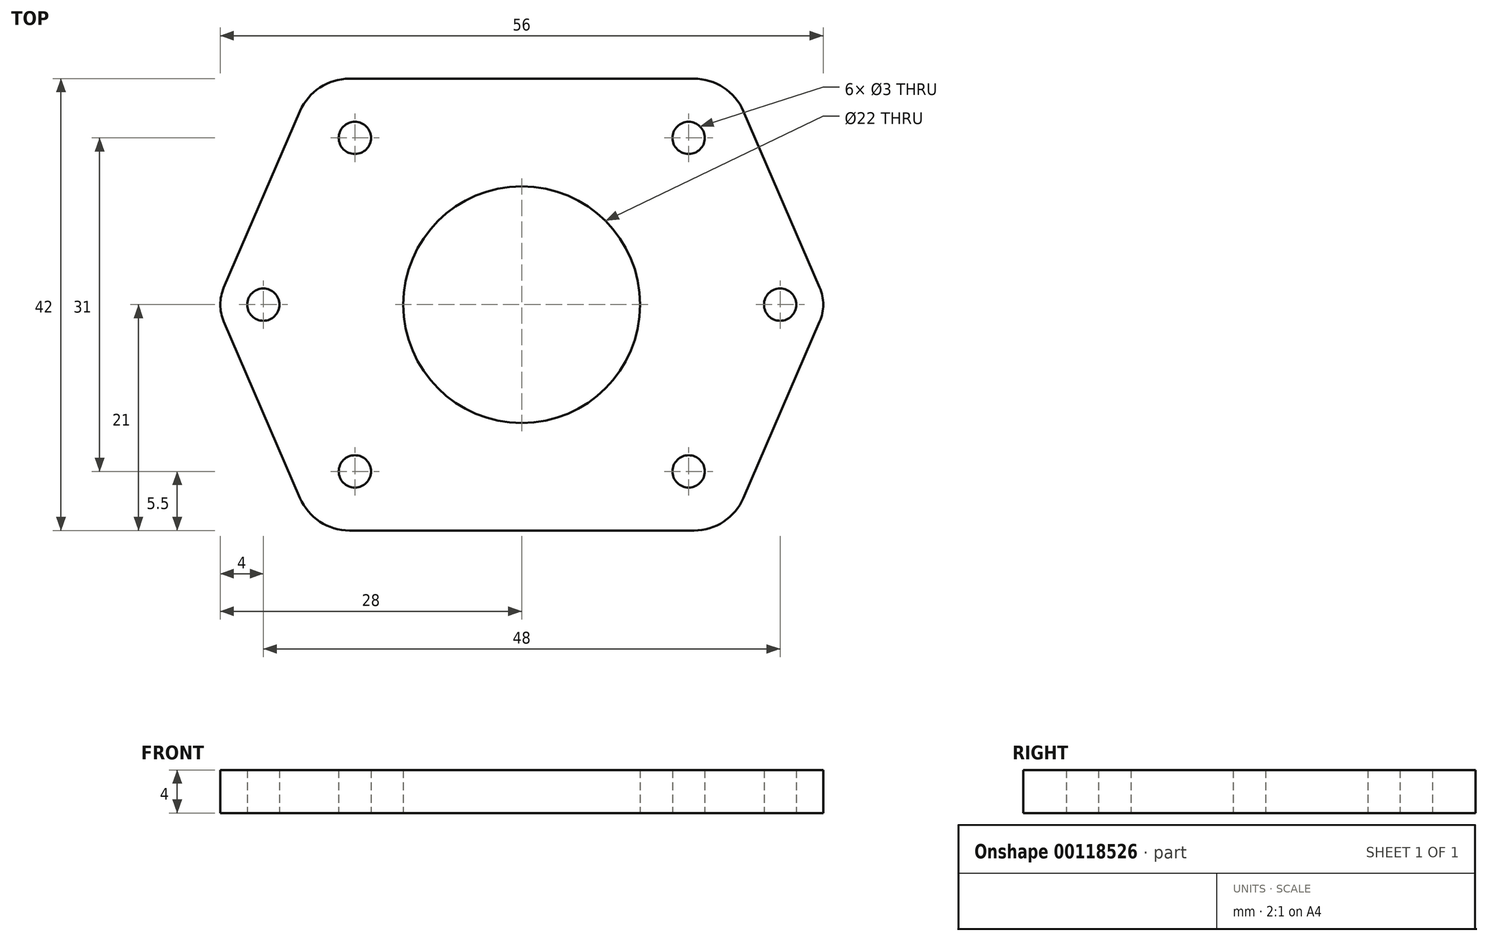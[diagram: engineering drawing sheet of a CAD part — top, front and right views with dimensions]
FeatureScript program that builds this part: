
annotation { "Feature Type Name" : "Feature", "Feature Type Description" : "" }
export const myFeature = defineFeature(function(context is Context, id is Id, definition is map)
    precondition{}
    {
        {
            var Q0;
            Q0=qCreatedBy(makeId("Top.planeOp"),FACE);
            var sketch = newSketch(context, id + "F0", { "sketchPlane" : qUnion([Q0])});
            skLineSegment(sketch, "E0.bottom", {"start": v(-15.5, 15.5) * mm, "end": v(15.5, 15.5) * mm, "construction": true});
            skLineSegment(sketch, "E0.top", {"start": v(-15.5, -15.5) * mm, "end": v(15.5, -15.5) * mm, "construction": true});
            skLineSegment(sketch, "E0.left", {"start": v(-15.5, 15.5) * mm, "end": v(-15.5, -15.5) * mm, "construction": true});
            skLineSegment(sketch, "E0.right", {"start": v(15.5, 15.5) * mm, "end": v(15.5, -15.5) * mm, "construction": true});
            skPoint(sketch, "E0.middle", {"position": v(0, 0) * mm});
            skCircle(sketch, "E1", {"center": v(-15.5, 15.5) * mm, "radius": 1.5 * mm});
            skCircle(sketch, "E2", {"center": v(15.5, 15.5) * mm, "radius": 1.5 * mm});
            skCircle(sketch, "E3", {"center": v(15.5, -15.5) * mm, "radius": 1.5 * mm});
            skCircle(sketch, "E4", {"center": v(-15.5, -15.5) * mm, "radius": 1.5 * mm});
            skCircle(sketch, "E5", {"center": v(0, 0) * mm, "radius": 11 * mm});
            skPoint(sketch, "E6.visualSharp", {"position": v(-21, -21) * mm});
            skPoint(sketch, "E7.visualSharp", {"position": v(21, -21) * mm});
            skCircle(sketch, "E8", {"center": v(-24, 0) * mm, "radius": 1.5 * mm});
            skCircle(sketch, "E9", {"center": v(24, 0) * mm, "radius": 1.5 * mm});
            skArc(sketch, "E10", {"start": v(-27.67, 1.59) * mm, "mid": v(-28, 0) * mm, "end": v(-27.67, -1.59) * mm});
            skArc(sketch, "E11", {"start": v(27.67, -1.59) * mm, "mid": v(28, 0) * mm, "end": v(27.67, 1.59) * mm});
            skLineSegment(sketch, "E12.bottom", {"start": v(-16, 21) * mm, "end": v(16, 21) * mm});
            skLineSegment(sketch, "E12.top", {"start": v(-16, -21) * mm, "end": v(16, -21) * mm});
            skPoint(sketch, "E13.visualSharp", {"position": v(-21, 21) * mm});
            skArc(sketch, "E13.filletArc", {"start": v(-16, 21) * mm, "mid": v(-18.75, 20.18) * mm, "end": v(-20.6, 17.98) * mm});
            skPoint(sketch, "E14.visualSharp", {"position": v(21, 21) * mm});
            skArc(sketch, "E14.filletArc", {"start": v(20.6, 17.98) * mm, "mid": v(18.75, 20.18) * mm, "end": v(16, 21) * mm});
            skArc(sketch, "E15.filletArc", {"start": v(16, -21) * mm, "mid": v(18.75, -20.18) * mm, "end": v(20.6, -17.98) * mm});
            skArc(sketch, "E16.filletArc", {"start": v(-20.6, -17.98) * mm, "mid": v(-18.75, -20.18) * mm, "end": v(-16, -21) * mm});
            skLineSegment(sketch, "E17", {"start": v(-20.6, 17.98) * mm, "end": v(-27.67, 1.59) * mm});
            skLineSegment(sketch, "E18", {"start": v(-20.6, -17.98) * mm, "end": v(-27.67, -1.59) * mm});
            skLineSegment(sketch, "E19", {"start": v(20.6, 17.98) * mm, "end": v(27.67, 1.59) * mm});
            skLineSegment(sketch, "E20", {"start": v(27.67, -1.59) * mm, "end": v(20.6, -17.98) * mm});
            skSolve(sketch);
        }
        {
            var Q0;
            Q0=makeQuery(id+"F0.imprint","IMPRINT",FACE,{"disambiguationData":[TD([[makeQuery(id+"F0.imprint","IMPRINT",EDGE,{"derivedFrom":sQuery(id+"F0.wireOp",EDGE,"E1")}),-1.0]])]});
            extrude(context, id + "F1", {"entities" : qUnion([Q0]), "depth" : 4 * mm});
        }
    });
